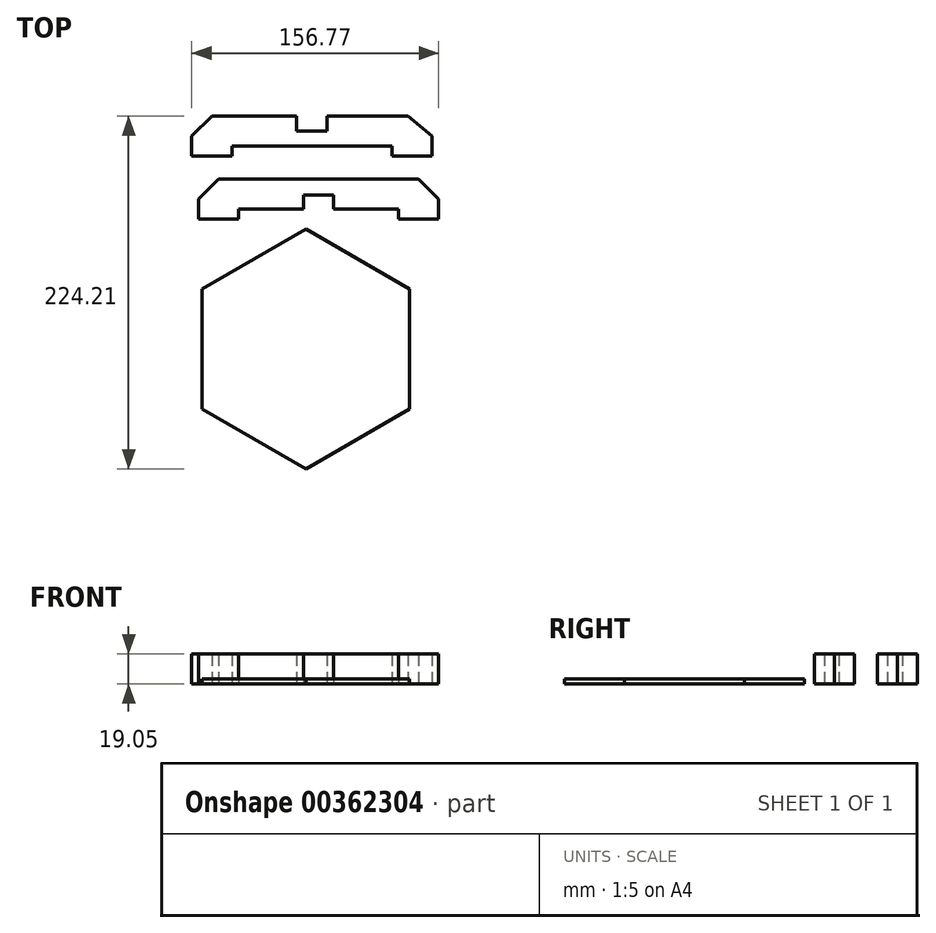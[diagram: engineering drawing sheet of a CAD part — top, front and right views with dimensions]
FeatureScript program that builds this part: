
annotation { "Feature Type Name" : "Feature", "Feature Type Description" : "" }
export const myFeature = defineFeature(function(context is Context, id is Id, definition is map)
    precondition{}
    {
        {
            var Q0;
            Q0=qCreatedBy(makeId("Top.planeOp"),FACE);
            var sketch = newSketch(context, id + "F0", { "sketchPlane" : qUnion([Q0])});
            skLineSegment(sketch, "E0.bottom", {"start": v(-52.78, 6.35) * mm, "end": v(74.22, 6.35) * mm});
            skLineSegment(sketch, "E0.top", {"start": v(-65.48, -19.05) * mm, "end": v(-40.08, -19.05) * mm});
            skLineSegment(sketch, "E0.left", {"start": v(-65.48, -6.35) * mm, "end": v(-65.48, -19.05) * mm});
            skLineSegment(sketch, "E0.right", {"start": v(86.92, -6.35) * mm, "end": v(86.92, -19.05) * mm});
            skLineSegment(sketch, "E1", {"start": v(-52.78, 6.35) * mm, "end": v(-65.48, -6.35) * mm});
            skLineSegment(sketch, "E2", {"start": v(74.22, 6.35) * mm, "end": v(86.92, -6.35) * mm});
            skPoint(sketch, "E3.orphan", {"position": v(-65.48, 6.35) * mm});
            skPoint(sketch, "E4.orphan", {"position": v(86.92, 6.35) * mm});
            skLineSegment(sketch, "E5", {"start": v(86.92, -19.05) * mm, "end": v(61.52, -19.05) * mm});
            skLineSegment(sketch, "E6", {"start": v(61.52, -19.05) * mm, "end": v(61.52, -12.7) * mm});
            skLineSegment(sketch, "E7", {"start": v(61.52, -12.7) * mm, "end": v(20.24, -12.7) * mm});
            skLineSegment(sketch, "E8", {"start": v(-40.08, -12.7) * mm, "end": v(-40.08, -19.05) * mm});
            skLineSegment(sketch, "E9.trimOffspring", {"start": v(1.2, -12.7) * mm, "end": v(-40.08, -12.7) * mm});
            skLineSegment(sketch, "E10.trimOffspring", {"start": v(61.52, -19.05) * mm, "end": v(86.92, -19.05) * mm});
            skPoint(sketch, "E11.start.orphan", {"position": v(10.72, -12.7) * mm});
            skPoint(sketch, "E12.start.orphan", {"position": v(4.37, 0) * mm});
            skPoint(sketch, "E13.start.orphan", {"position": v(10.72, 0) * mm});
            skLineSegment(sketch, "E14.0", {"start": v(1.2, -12.7) * mm, "end": v(1.2, -3.68) * mm});
            skLineSegment(sketch, "E15.0", {"start": v(20.24, -3.68) * mm, "end": v(20.24, -12.7) * mm});
            skLineSegment(sketch, "E16", {"start": v(1.2, -3.68) * mm, "end": v(20.24, -3.68) * mm});
            skSolve(sketch);
        }
        {
            var Q0;
            Q0=makeQuery(id+"F0.imprint","IMPRINT",FACE,{"disambiguationData":[TD([[makeQuery(id+"F0.imprint","IMPRINT",EDGE,{"derivedFrom":sQuery(id+"F0.wireOp",EDGE,"E0.bottom")}),-1.0]])]});
            extrude(context, id + "F1", {"entities" : qUnion([Q0]), "depth" : 19.05 * mm});
        }
        {
            var Q0;
            Q0=qCreatedBy(makeId("Top.planeOp"),FACE);
            var sketch = newSketch(context, id + "F2", { "sketchPlane" : qUnion([Q0])});
            skLineSegment(sketch, "E17.bottom", {"start": v(-57.15, 46.4) * mm, "end": v(-44.5, 46.4) * mm});
            skLineSegment(sketch, "E17.left", {"start": v(-69.85, 33.7) * mm, "end": v(-69.85, 21) * mm});
            skLineSegment(sketch, "E17.right", {"start": v(82.55, 33.7) * mm, "end": v(82.55, 21) * mm});
            skLineSegment(sketch, "E18.left", {"start": v(-69.85, 46.4) * mm, "end": v(-69.85, 46.4) * mm});
            skLineSegment(sketch, "E18.right", {"start": v(-57.15, 46.4) * mm, "end": v(-57.15, 46.4) * mm});
            skLineSegment(sketch, "E19", {"start": v(-57.15, 46.4) * mm, "end": v(-69.85, 33.7) * mm});
            skLineSegment(sketch, "E20", {"start": v(67.52, 46.4) * mm, "end": v(82.55, 33.7) * mm});
            skPoint(sketch, "E21.orphan", {"position": v(82.55, 46.4) * mm});
            skLineSegment(sketch, "E22", {"start": v(-69.85, 21) * mm, "end": v(-44.45, 21) * mm});
            skLineSegment(sketch, "E23", {"start": v(-44.45, 21) * mm, "end": v(-44.45, 27.36) * mm});
            skLineSegment(sketch, "E24", {"start": v(-44.45, 27.36) * mm, "end": v(57.15, 27.36) * mm});
            skLineSegment(sketch, "E25", {"start": v(57.15, 27.36) * mm, "end": v(57.15, 21) * mm});
            skLineSegment(sketch, "E26", {"start": v(57.15, 21) * mm, "end": v(82.55, 21) * mm});
            skLineSegment(sketch, "E27", {"start": v(-57.15, 46.4) * mm, "end": v(-3.17, 46.4) * mm});
            skLineSegment(sketch, "E28.trimOffspring", {"start": v(15.88, 46.4) * mm, "end": v(67.52, 46.4) * mm});
            skLineSegment(sketch, "E29.0", {"start": v(15.88, 36.88) * mm, "end": v(15.88, 46.4) * mm});
            skLineSegment(sketch, "E30.0", {"start": v(-3.18, 46.4) * mm, "end": v(-3.17, 36.88) * mm});
            skLineSegment(sketch, "E31", {"start": v(15.88, 36.88) * mm, "end": v(-3.17, 36.88) * mm});
            skPoint(sketch, "E32.end.orphan", {"position": v(12.7, 46.4) * mm});
            skPoint(sketch, "E33.orphan", {"position": v(0, 46.4) * mm});
            skSolve(sketch);
        }
        {
            var Q0;
            Q0=makeQuery(id+"F2.imprint","IMPRINT",FACE,{"disambiguationData":[TD([[makeQuery(id+"F2.imprint","IMPRINT",EDGE,{"derivedFrom":sQuery(id+"F2.wireOp",EDGE,"E17.left")}),1.0]])]});
            extrude(context, id + "F3", {"entities" : qUnion([Q0]), "depth" : 19.05 * mm});
        }
        {
            var Q0;
            Q0=qCreatedBy(makeId("Top.planeOp"),FACE);
            var sketch = newSketch(context, id + "F4", { "sketchPlane" : qUnion([Q0])});
            skPoint(sketch, "E34.center", {"position": v(0, 0) * mm});
            skLineSegment(sketch, "E35", {"start": v(2.54, -25.4) * mm, "end": v(68.53, -63.5) * mm});
            skLineSegment(sketch, "E36", {"start": v(68.53, -63.5) * mm, "end": v(68.53, -139.7) * mm});
            skLineSegment(sketch, "E37", {"start": v(68.53, -139.7) * mm, "end": v(2.54, -177.8) * mm});
            skLineSegment(sketch, "E38", {"start": v(-63.45, -139.7) * mm, "end": v(2.54, -177.8) * mm});
            skLineSegment(sketch, "E39", {"start": v(-63.45, -63.5) * mm, "end": v(-63.45, -139.7) * mm});
            skLineSegment(sketch, "E40", {"start": v(-63.45, -63.5) * mm, "end": v(2.54, -25.4) * mm});
            skSolve(sketch);
        }
        {
            var Q0;
            Q0 = qSketchRegion(id + "F4", true);
            extrude(context, id + "F5", {"entities" : qUnion([Q0]), "depth" : 3.17 * mm});
        }
    });
